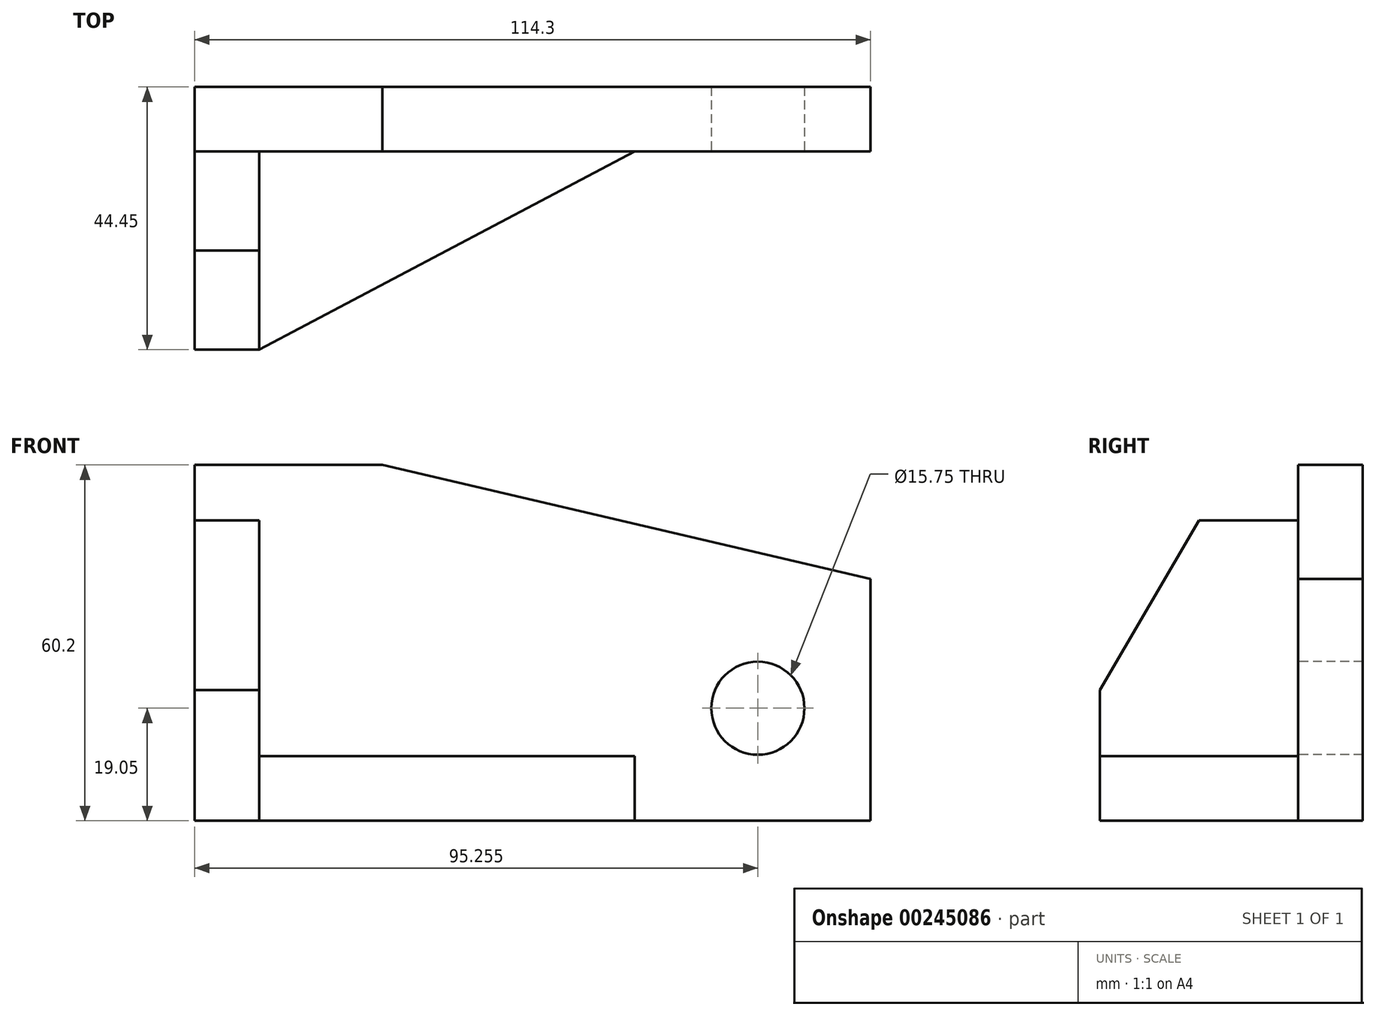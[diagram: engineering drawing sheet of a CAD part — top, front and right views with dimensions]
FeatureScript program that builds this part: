
annotation { "Feature Type Name" : "Feature", "Feature Type Description" : "" }
export const myFeature = defineFeature(function(context is Context, id is Id, definition is map)
    precondition{}
    {
        {
            var Q0;
            Q0=qCreatedBy(makeId("Top.planeOp"),FACE);
            var sketch = newSketch(context, id + "F0", { "sketchPlane" : qUnion([Q0])});
            skLineSegment(sketch, "E0.bottom", {"start": v(-81.84, -4.78) * mm, "end": v(32.46, -4.78) * mm});
            skLineSegment(sketch, "E0.top", {"start": v(-81.84, -15.7) * mm, "end": v(32.46, -15.7) * mm});
            skLineSegment(sketch, "E0.left", {"start": v(-81.84, -4.78) * mm, "end": v(-81.84, -15.7) * mm});
            skLineSegment(sketch, "E0.right", {"start": v(32.46, -4.78) * mm, "end": v(32.46, -15.7) * mm});
            skPoint(sketch, "E1", {"position": v(-50.09, -4.78) * mm});
            skPoint(sketch, "E2", {"position": v(-50.09, -15.7) * mm});
            skLineSegment(sketch, "E3", {"start": v(-50.09, -15.7) * mm, "end": v(-50.09, -4.78) * mm});
            skLineSegment(sketch, "E4", {"start": v(-81.84, -4.78) * mm, "end": v(-81.84, -49.23) * mm});
            skLineSegment(sketch, "E5", {"start": v(-81.84, -4.78) * mm, "end": v(-70.91, -4.78) * mm});
            skLineSegment(sketch, "E6", {"start": v(-81.84, -49.23) * mm, "end": v(-70.91, -49.23) * mm});
            skLineSegment(sketch, "E7", {"start": v(-70.91, -49.23) * mm, "end": v(-7.41, -15.7) * mm});
            skPoint(sketch, "E8", {"position": v(-70.91, -15.7) * mm});
            skLineSegment(sketch, "E9", {"start": v(-70.91, -15.7) * mm, "end": v(-70.91, -49.23) * mm});
            skSolve(sketch);
        }
        {
            var Q0;
            {var subQ0=sQuery(id+"F0.wireOp",EDGE,"E3");Q0=makeQuery(id+"F0.imprint","IMPRINT",FACE,{"disambiguationData":[TD([[makeQuery(id+"F0.imprint","IMPRINT",EDGE,{"derivedFrom":subQ0}),1.0]])]});}
            extrude(context, id + "F1", {"entities" : qUnion([Q0]), "depth" : 60.2 * mm});
        }
        {
            var Q0;
            {var subQ0=sQuery(id+"F0.wireOp",EDGE,"E0.right");Q0=makeQuery(id+"F0.imprint","IMPRINT",FACE,{"disambiguationData":[TD([[makeQuery(id+"F0.imprint","IMPRINT",EDGE,{"derivedFrom":subQ0}),-1.0]])]});}
            extrude(context, id + "F2", {"entities" : qUnion([Q0]), "operationType" : NewBodyOperationType.ADD, "depth" : 60.2 * mm});
        }
        {
            var Q0;
            {var subQ4=sQuery(id+"F0.wireOp",EDGE,"E6");Q0=makeQuery(id+"F0.imprint","IMPRINT",FACE,{"disambiguationData":[TD([[makeQuery(id+"F0.imprint","IMPRINT",EDGE,{"derivedFrom":subQ4}),1.0]])]});}
            extrude(context, id + "F3", {"entities" : qUnion([Q0]), "operationType" : NewBodyOperationType.ADD, "depth" : 50.8 * mm});
        }
        {
            var Q0;
            {var subQ3=sQuery(id+"F0.wireOp",EDGE,"E7");Q0=makeQuery(id+"F0.imprint","IMPRINT",FACE,{"disambiguationData":[TD([[makeQuery(id+"F0.imprint","IMPRINT",EDGE,{"derivedFrom":subQ3}),1.0]])]});}
            extrude(context, id + "F4", {"entities" : qUnion([Q0]), "operationType" : NewBodyOperationType.ADD, "depth" : 10.92 * mm});
        }
        {
            var Q0;
            {var subQ0=sQuery(id+"F0.wireOp",EDGE,"E0.top");Q0=makeQuery(id+"F2.boolean.opBoolean","MERGE",FACE,{"derivedFrom":[makeQuery(id+"F1.opExtrude","SWEPT_FACE",FACE,{"disambiguationData":[OSD([subQ0])]}),makeQuery(id+"F2.opExtrude","SWEPT_FACE",FACE,{"disambiguationData":[OSD([subQ0])]})]});}
            var sketch = newSketch(context, id + "F5", { "sketchPlane" : qUnion([Q0])});
            skPoint(sketch, "E10", {"position": v(-50.09, 60.2) * mm});
            skPoint(sketch, "E11", {"position": v(32.46, 60.2) * mm});
            skPoint(sketch, "E12", {"position": v(32.46, 0) * mm});
            skCircle(sketch, "E13", {"center": v(13.41, 19.05) * mm, "radius": 7.87 * mm});
            skPoint(sketch, "E14", {"position": v(32.46, 19.05) * mm});
            skPoint(sketch, "E15", {"position": v(12.53, 0) * mm});
            skLineSegment(sketch, "E16", {"start": v(-50.09, 60.2) * mm, "end": v(32.46, 40.9) * mm});
            skPoint(sketch, "E17", {"position": v(-50.09, 40.9) * mm});
            skLineSegment(sketch, "E18", {"start": v(-50.09, 40.9) * mm, "end": v(-50.09, 60.2) * mm});
            skLineSegment(sketch, "E19", {"start": v(-50.09, 40.9) * mm, "end": v(32.46, 40.9) * mm});
            skLineSegment(sketch, "E20", {"start": v(-50.09, 60.2) * mm, "end": v(32.46, 60.2) * mm});
            skLineSegment(sketch, "E21", {"start": v(32.46, 40.9) * mm, "end": v(32.46, 60.2) * mm});
            skSolve(sketch);
        }
        {
            var Q0;
            Q0=makeQuery(id+"F5.imprint","IMPRINT",FACE,{"disambiguationData":[TD([[makeQuery(id+"F5.imprint","IMPRINT",EDGE,{"derivedFrom":sQuery(id+"F5.wireOp",EDGE,"E13")}),1.0]])]});
            extrude(context, id + "F6", {"entities" : qUnion([Q0]), "operationType" : NewBodyOperationType.REMOVE, "endBound" : BoundingType.THROUGH_ALL, "oppositeDirection" : true, "depth" : 25.4 * mm});
        }
        {
            var Q0;
            Q0=makeQuery(id+"F5.imprint","IMPRINT",FACE,{"disambiguationData":[TD([[makeQuery(id+"F5.imprint","IMPRINT",EDGE,{"derivedFrom":sQuery(id+"F5.wireOp",EDGE,"E16")}),1.0]])]});
            extrude(context, id + "F7", {"entities" : qUnion([Q0]), "operationType" : NewBodyOperationType.REMOVE, "oppositeDirection" : true, "depth" : 25.4 * mm});
        }
        {
            var Q0;
            {var subQ0=sQuery(id+"F0.wireOp",EDGE,"E4");Q0=makeQuery(id+"F3.boolean.opBoolean","MERGE",FACE,{"derivedFrom":[makeQuery(id+"F1.opExtrude","SWEPT_FACE",FACE,{"disambiguationData":[OSD([subQ0])]}),makeQuery(id+"F3.opExtrude","SWEPT_FACE",FACE,{"disambiguationData":[OSD([subQ0])]})]});}
            var sketch = newSketch(context, id + "F8", { "sketchPlane" : qUnion([Q0])});
            skLineSegment(sketch, "E22", {"start": v(32.46, 50.8) * mm, "end": v(49.23, 22.1) * mm});
            skPoint(sketch, "E23", {"position": v(49.23, 0) * mm});
            skSolve(sketch);
        }
        {
            var Q0;
            {var subQ0=sQuery(id+"F8.wireOp",EDGE,"E22");Q0=makeQuery(id+"F8.imprint","IMPRINT",FACE,{"disambiguationData":[TD([[makeQuery(id+"F8.imprint","IMPRINT",EDGE,{"derivedFrom":subQ0}),1.0]])]});}
            extrude(context, id + "F9", {"entities" : qUnion([Q0]), "operationType" : NewBodyOperationType.REMOVE, "oppositeDirection" : true, "depth" : 25.4 * mm});
        }
    });
